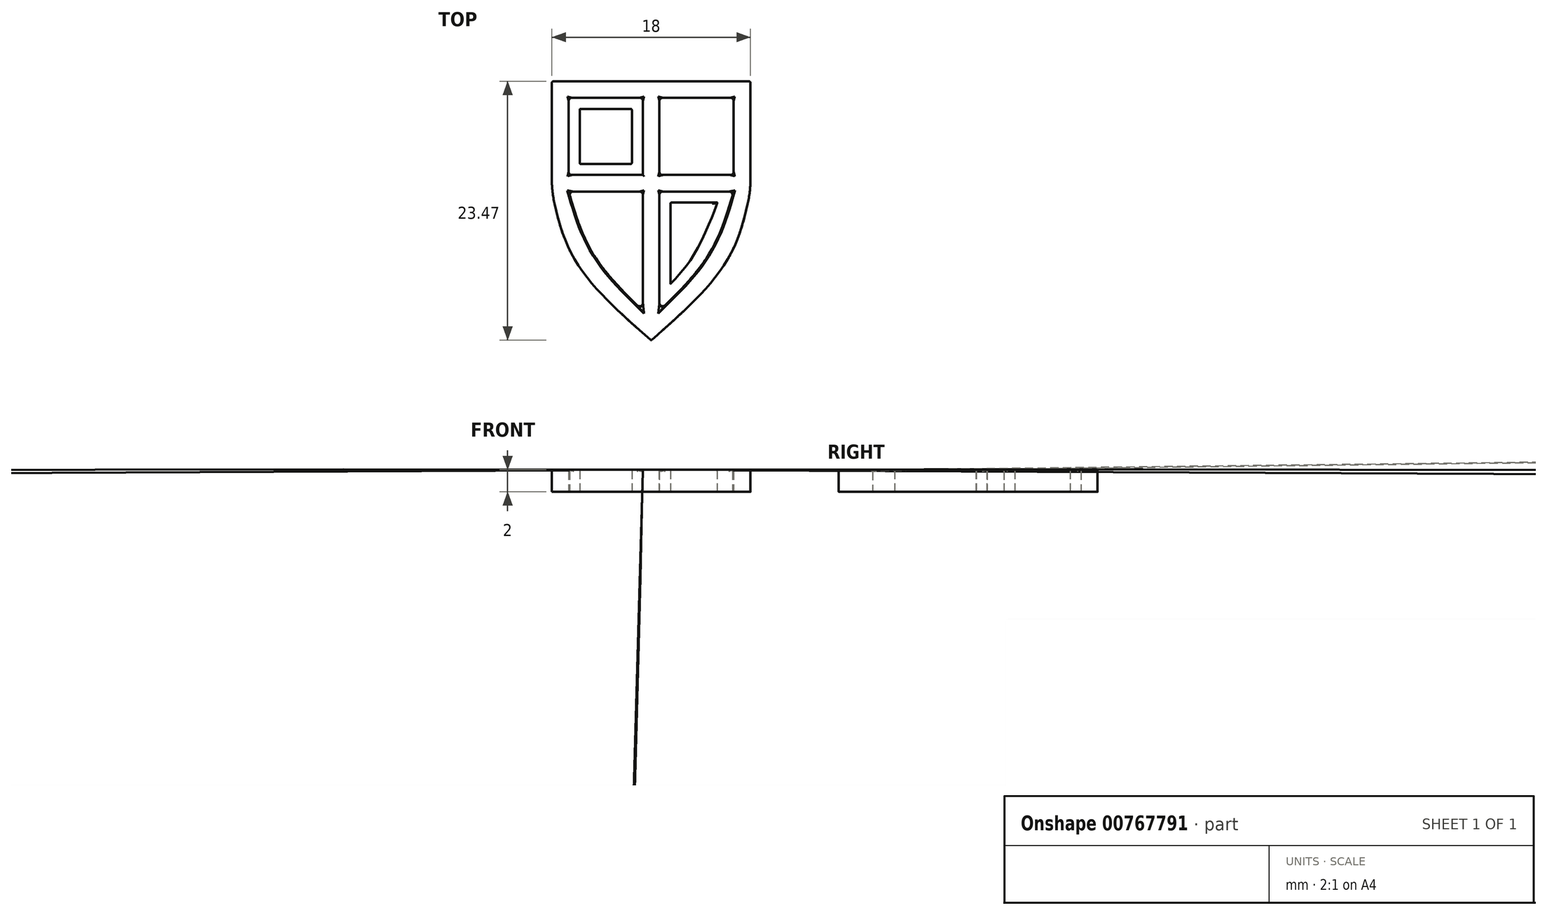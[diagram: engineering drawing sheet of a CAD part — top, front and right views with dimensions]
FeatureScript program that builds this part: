
annotation { "Feature Type Name" : "Feature", "Feature Type Description" : "" }
export const myFeature = defineFeature(function(context is Context, id is Id, definition is map)
    precondition{}
    {
        {
            var Q0;
            Q0=qCreatedBy(makeId("Top.planeOp"),FACE);
            var sketch = newSketch(context, id + "F0", { "sketchPlane" : qUnion([Q0])});
            skLineSegment(sketch, "E0.left", {"start": v(9, 10) * mm, "end": v(9, 0) * mm});
            skLineSegment(sketch, "E0.right", {"start": v(-9, 10) * mm, "end": v(-9, 0) * mm});
            skPoint(sketch, "E0.middle", {"position": v(0, 0) * mm});
            skLineSegment(sketch, "E1.top", {"start": v(7.48, 8.5) * mm, "end": v(0.75, 8.5) * mm});
            skLineSegment(sketch, "E1.right", {"start": v(-7.48, 1.5) * mm, "end": v(-7.48, 8.5) * mm});
            skLineSegment(sketch, "E2", {"start": v(-7.48, 0) * mm, "end": v(-0.75, 0) * mm});
            skLineSegment(sketch, "E3", {"start": v(-7.48, 1.5) * mm, "end": v(-0.75, 1.5) * mm});
            skLineSegment(sketch, "E4", {"start": v(-0.75, 8.5) * mm, "end": v(-0.75, 1.5) * mm});
            skLineSegment(sketch, "E5", {"start": v(0.75, 8.5) * mm, "end": v(0.75, 1.5) * mm});
            skFitSpline(sketch, "E6", {"points": [v(0, -13.5) * mm, v(6.85, -6.3) * mm, v(9, 0) * mm], "startDerivative": vector(14.56, 12.85) * mm, "endDerivative": vector(3.06, 14.2) * mm});
            skPoint(sketch, "E7.0.internal.snap0", {"position": v(0, -8.5) * mm});
            skFitSpline(sketch, "E7", {"points": [v(0, -11.52) * mm, v(5.23, -5.7) * mm, v(7.48, 0) * mm], "startDerivative": vector(11.2, 10.69) * mm, "endDerivative": vector(3.65, 12.4) * mm});
            skFitSpline(sketch, "E8.MirrorCS", {"points": [v(0, -11.52) * mm, v(-5.23, -5.7) * mm, v(-7.48, 0) * mm], "startDerivative": vector(-11.2, 10.69) * mm, "endDerivative": vector(-3.65, 12.4) * mm});
            skFitSpline(sketch, "E9.MirrorCS", {"points": [v(0, -13.5) * mm, v(-6.85, -6.3) * mm, v(-9, 0) * mm], "startDerivative": vector(-14.56, 12.85) * mm, "endDerivative": vector(-3.06, 14.2) * mm});
            skLineSegment(sketch, "E10.trimOffspring", {"start": v(7.48, 1.5) * mm, "end": v(7.48, 8.5) * mm});
            skPoint(sketch, "E11.orphan", {"position": v(7.48, -8.5) * mm});
            skPoint(sketch, "E12.orphan", {"position": v(9, -13.5) * mm});
            skPoint(sketch, "E13.orphan", {"position": v(-7.48, -8.5) * mm});
            skPoint(sketch, "E0.top.end.orphan", {"position": v(-9, -13.5) * mm});
            skLineSegment(sketch, "E14.trimOffspring", {"start": v(0.75, 0) * mm, "end": v(0.75, -10.8) * mm});
            skLineSegment(sketch, "E15.trimOffspring", {"start": v(0.75, 1.5) * mm, "end": v(7.48, 1.5) * mm});
            skLineSegment(sketch, "E16.trimOffspring", {"start": v(-0.75, 0) * mm, "end": v(-0.75, -10.8) * mm});
            skLineSegment(sketch, "E17.trimOffspring", {"start": v(0.75, 0) * mm, "end": v(7.48, 0) * mm});
            skLineSegment(sketch, "E18.trimOffspring", {"start": v(-0.75, 8.5) * mm, "end": v(-7.48, 8.5) * mm});
            skLineSegment(sketch, "E19", {"start": v(-9, 10) * mm, "end": v(9, 10) * mm});
            skPoint(sketch, "E0.bottom.start.orphan", {"position": v(9, 13.5) * mm});
            skPoint(sketch, "E20.orphan", {"position": v(-9, 13.5) * mm});
            skLineSegment(sketch, "E21.bottom", {"start": v(-6.48, 7.5) * mm, "end": v(-1.75, 7.5) * mm});
            skLineSegment(sketch, "E21.top", {"start": v(-6.48, 2.5) * mm, "end": v(-1.75, 2.5) * mm});
            skLineSegment(sketch, "E21.left", {"start": v(-6.48, 7.5) * mm, "end": v(-6.48, 2.5) * mm});
            skLineSegment(sketch, "E21.right", {"start": v(-1.75, 7.5) * mm, "end": v(-1.75, 2.5) * mm});
            skLineSegment(sketch, "E22.bottom", {"start": v(1.75, -1) * mm, "end": v(6, -1) * mm});
            skLineSegment(sketch, "E22.left", {"start": v(1.75, -1) * mm, "end": v(1.75, -8.38) * mm});
            skFitSpline(sketch, "E23", {"points": [v(1.75, -8.38) * mm, v(4.29, -5) * mm, v(6, -1) * mm, v(6, -1) * mm], "startDerivative": vector(5.12, 5.41) * mm, "endDerivative": vector(-0.07, -0.03) * mm});
            skSolve(sketch);
        }
        {
            var Q0;
            Q0=makeQuery(id+"F0.imprint","IMPRINT",FACE,{"disambiguationData":[TD([[makeQuery(id+"F0.imprint","IMPRINT",EDGE,{"derivedFrom":sQuery(id+"F0.wireOp",EDGE,"E0.left")}),-1.0]])]});
            var Q1;
            Q1=makeQuery(id+"F0.imprint","IMPRINT",FACE,{"disambiguationData":[TD([[makeQuery(id+"F0.imprint","IMPRINT",EDGE,{"derivedFrom":sQuery(id+"F0.wireOp",EDGE,"E21.bottom")}),-1.0]])]});
            var Q2;
            Q2=makeQuery(id+"F0.imprint","IMPRINT",FACE,{"disambiguationData":[TD([[makeQuery(id+"F0.imprint","IMPRINT",EDGE,{"derivedFrom":sQuery(id+"F0.wireOp",EDGE,"E22.bottom")}),-1.0]])]});
            extrude(context, id + "F1", {"entities" : qUnion([Q0, Q1, Q2]), "depth" : 2 * mm, "offsetDistance" : 25 * mm});
        }
        {
            var Q0;
            Q0=makeQuery(id+"F1.opExtrude","CAP_FACE",FACE,{"disambiguationData":[OSD([sQuery(id+"F0.wireOp",EDGE,"E0.left"),sQuery(id+"F0.wireOp",EDGE,"E0.right"),sQuery(id+"F0.wireOp",EDGE,"E1.top"),sQuery(id+"F0.wireOp",EDGE,"E1.right"),sQuery(id+"F0.wireOp",EDGE,"E2"),sQuery(id+"F0.wireOp",EDGE,"E3"),sQuery(id+"F0.wireOp",EDGE,"E4"),sQuery(id+"F0.wireOp",EDGE,"E5"),sQuery(id+"F0.wireOp",EDGE,"E6"),sQuery(id+"F0.wireOp",EDGE,"E7"),sQuery(id+"F0.wireOp",EDGE,"E8.MirrorCS"),sQuery(id+"F0.wireOp",EDGE,"E9.MirrorCS"),sQuery(id+"F0.wireOp",EDGE,"E10.trimOffspring"),sQuery(id+"F0.wireOp",EDGE,"E14.trimOffspring"),sQuery(id+"F0.wireOp",EDGE,"E15.trimOffspring"),sQuery(id+"F0.wireOp",EDGE,"E16.trimOffspring"),sQuery(id+"F0.wireOp",EDGE,"E17.trimOffspring"),sQuery(id+"F0.wireOp",EDGE,"E18.trimOffspring"),sQuery(id+"F0.wireOp",EDGE,"E19")])],"isStart":false});
            var Q1;
            Q1=makeQuery(id+"F1.opExtrude","CAP_FACE",FACE,{"disambiguationData":[OSD([sQuery(id+"F0.wireOp",EDGE,"E21.bottom"),sQuery(id+"F0.wireOp",EDGE,"E21.top"),sQuery(id+"F0.wireOp",EDGE,"E21.left"),sQuery(id+"F0.wireOp",EDGE,"E21.right")])],"isStart":false});
            var Q2;
            Q2=makeQuery(id+"F1.opExtrude","CAP_EDGE",EDGE,{"disambiguationData":[OSD([sQuery(id+"F0.wireOp",EDGE,"E22.bottom")])],"isStart":false});
            var Q3;
            Q3=makeQuery(id+"F1.opExtrude","CAP_EDGE",EDGE,{"disambiguationData":[OSD([sQuery(id+"F0.wireOp",EDGE,"E22.left")])],"isStart":false});
            fillet(context, id + "F2", {"entities" : qUnion([Q0, Q1, Q2, Q3]), "radius" : 0.1 * mm, "tangentPropagation" : true, "allowEdgeOverflow" : false});
        }
        {
            var Q0;
            Q0=makeQuery(id+"F1.opExtrude","SWEPT_EDGE",EDGE,{"disambiguationData":[OSD([sQuery(id+"F0.wireOp",EDGE,"E0.left"),sQuery(id+"F0.wireOp",EDGE,"E6")])]});
            var Q1;
            Q1=makeQuery(id+"F1.opExtrude","SWEPT_EDGE",EDGE,{"disambiguationData":[OSD([sQuery(id+"F0.wireOp",EDGE,"E0.right"),sQuery(id+"F0.wireOp",EDGE,"E9.MirrorCS")])]});
            fillet(context, id + "F3", {"entities" : qUnion([Q0, Q1]), "radius" : 10 * mm, "tangentPropagation" : true, "allowEdgeOverflow" : false});
        }
        {
            var Q0;
            Q0=makeQuery(id+"F1.opExtrude","SWEPT_EDGE",EDGE,{"disambiguationData":[OSD([sQuery(id+"F0.wireOp",EDGE,"E2"),sQuery(id+"F0.wireOp",EDGE,"E8.MirrorCS")])]});
            var Q1;
            Q1=makeQuery(id+"F1.opExtrude","SWEPT_EDGE",EDGE,{"disambiguationData":[OSD([sQuery(id+"F0.wireOp",EDGE,"E7"),sQuery(id+"F0.wireOp",EDGE,"E17.trimOffspring")])]});
            var Q2;
            Q2=makeQuery(id+"F1.opExtrude","SWEPT_EDGE",EDGE,{"disambiguationData":[OSD([sQuery(id+"F0.wireOp",EDGE,"E2"),sQuery(id+"F0.wireOp",EDGE,"E16.trimOffspring")])]});
            var Q3;
            Q3=makeQuery(id+"F1.opExtrude","SWEPT_EDGE",EDGE,{"disambiguationData":[OSD([sQuery(id+"F0.wireOp",EDGE,"E14.trimOffspring"),sQuery(id+"F0.wireOp",EDGE,"E17.trimOffspring")])]});
            var Q4;
            Q4=makeQuery(id+"F1.opExtrude","SWEPT_EDGE",EDGE,{"disambiguationData":[OSD([sQuery(id+"F0.wireOp",EDGE,"E1.top"),sQuery(id+"F0.wireOp",EDGE,"E5")])]});
            var Q5;
            Q5=makeQuery(id+"F1.opExtrude","SWEPT_EDGE",EDGE,{"disambiguationData":[OSD([sQuery(id+"F0.wireOp",EDGE,"E1.right"),sQuery(id+"F0.wireOp",EDGE,"E18.trimOffspring")])]});
            var Q6;
            Q6=makeQuery(id+"F1.opExtrude","SWEPT_EDGE",EDGE,{"disambiguationData":[OSD([sQuery(id+"F0.wireOp",EDGE,"E1.top"),sQuery(id+"F0.wireOp",EDGE,"E10.trimOffspring")])]});
            var Q7;
            Q7=makeQuery(id+"F1.opExtrude","SWEPT_EDGE",EDGE,{"disambiguationData":[OSD([sQuery(id+"F0.wireOp",EDGE,"E4"),sQuery(id+"F0.wireOp",EDGE,"E18.trimOffspring")])]});
            var Q8;
            Q8=makeQuery(id+"F1.opExtrude","SWEPT_EDGE",EDGE,{"disambiguationData":[OSD([sQuery(id+"F0.wireOp",EDGE,"E5"),sQuery(id+"F0.wireOp",EDGE,"E15.trimOffspring")])]});
            var Q9;
            Q9=makeQuery(id+"F1.opExtrude","SWEPT_EDGE",EDGE,{"disambiguationData":[OSD([sQuery(id+"F0.wireOp",EDGE,"E1.right"),sQuery(id+"F0.wireOp",EDGE,"E3")])]});
            var Q10;
            Q10=makeQuery(id+"F1.opExtrude","SWEPT_EDGE",EDGE,{"disambiguationData":[OSD([sQuery(id+"F0.wireOp",EDGE,"E7"),sQuery(id+"F0.wireOp",EDGE,"E14.trimOffspring")])]});
            var Q11;
            Q11=makeQuery(id+"F1.opExtrude","SWEPT_EDGE",EDGE,{"disambiguationData":[OSD([sQuery(id+"F0.wireOp",EDGE,"E8.MirrorCS"),sQuery(id+"F0.wireOp",EDGE,"E16.trimOffspring")])]});
            var Q12;
            Q12=makeQuery(id+"F1.opExtrude","SWEPT_EDGE",EDGE,{"disambiguationData":[OSD([sQuery(id+"F0.wireOp",EDGE,"E10.trimOffspring"),sQuery(id+"F0.wireOp",EDGE,"E15.trimOffspring")])]});
            fillet(context, id + "F4", {"entities" : qUnion([Q0, Q1, Q2, Q3, Q4, Q5, Q6, Q7, Q8, Q9, Q10, Q11, Q12]), "radius" : 0.3 * mm, "tangentPropagation" : true, "allowEdgeOverflow" : false});
        }
        {
            var Q0;
            Q0=makeQuery(id+"F1.opExtrude","SWEPT_EDGE",EDGE,{"disambiguationData":[OSD([sQuery(id+"F0.wireOp",EDGE,"E0.right"),sQuery(id+"F0.wireOp",EDGE,"E19")])]});
            var Q1;
            Q1=makeQuery(id+"F1.opExtrude","SWEPT_EDGE",EDGE,{"disambiguationData":[OSD([sQuery(id+"F0.wireOp",EDGE,"E0.left"),sQuery(id+"F0.wireOp",EDGE,"E19")])]});
            fillet(context, id + "F5", {"entities" : qUnion([Q0, Q1]), "radius" : 0.15 * mm, "tangentPropagation" : true, "allowEdgeOverflow" : false});
        }
        {
            var Q0;
            Q0=makeQuery(id+"F1.opExtrude","SWEPT_EDGE",EDGE,{"disambiguationData":[OSD([sQuery(id+"F0.wireOp",EDGE,"E6"),sQuery(id+"F0.wireOp",EDGE,"E9.MirrorCS")])]});
            var Q1;
            Q1=makeQuery(id+"F1.opExtrude","SWEPT_EDGE",EDGE,{"disambiguationData":[OSD([sQuery(id+"F0.wireOp",EDGE,"E22.bottom"),sQuery(id+"F0.wireOp",EDGE,"E23")])]});
            var Q2;
            Q2=makeQuery(id+"F1.opExtrude","SWEPT_EDGE",EDGE,{"disambiguationData":[OSD([sQuery(id+"F0.wireOp",EDGE,"E22.bottom"),sQuery(id+"F0.wireOp",EDGE,"E22.left")])]});
            var Q3;
            Q3=makeQuery(id+"F1.opExtrude","SWEPT_EDGE",EDGE,{"disambiguationData":[OSD([sQuery(id+"F0.wireOp",EDGE,"E21.top"),sQuery(id+"F0.wireOp",EDGE,"E21.right")])]});
            var Q4;
            Q4=makeQuery(id+"F1.opExtrude","SWEPT_EDGE",EDGE,{"disambiguationData":[OSD([sQuery(id+"F0.wireOp",EDGE,"E21.top"),sQuery(id+"F0.wireOp",EDGE,"E21.left")])]});
            var Q5;
            Q5=makeQuery(id+"F1.opExtrude","SWEPT_EDGE",EDGE,{"disambiguationData":[OSD([sQuery(id+"F0.wireOp",EDGE,"E21.bottom"),sQuery(id+"F0.wireOp",EDGE,"E21.left")])]});
            var Q6;
            Q6=makeQuery(id+"F1.opExtrude","SWEPT_EDGE",EDGE,{"disambiguationData":[OSD([sQuery(id+"F0.wireOp",EDGE,"E21.bottom"),sQuery(id+"F0.wireOp",EDGE,"E21.right")])]});
            fillet(context, id + "F6", {"entities" : qUnion([Q0, Q1, Q2, Q3, Q4, Q5, Q6]), "radius" : 0.1 * mm, "tangentPropagation" : true, "allowEdgeOverflow" : false});
        }
    });
